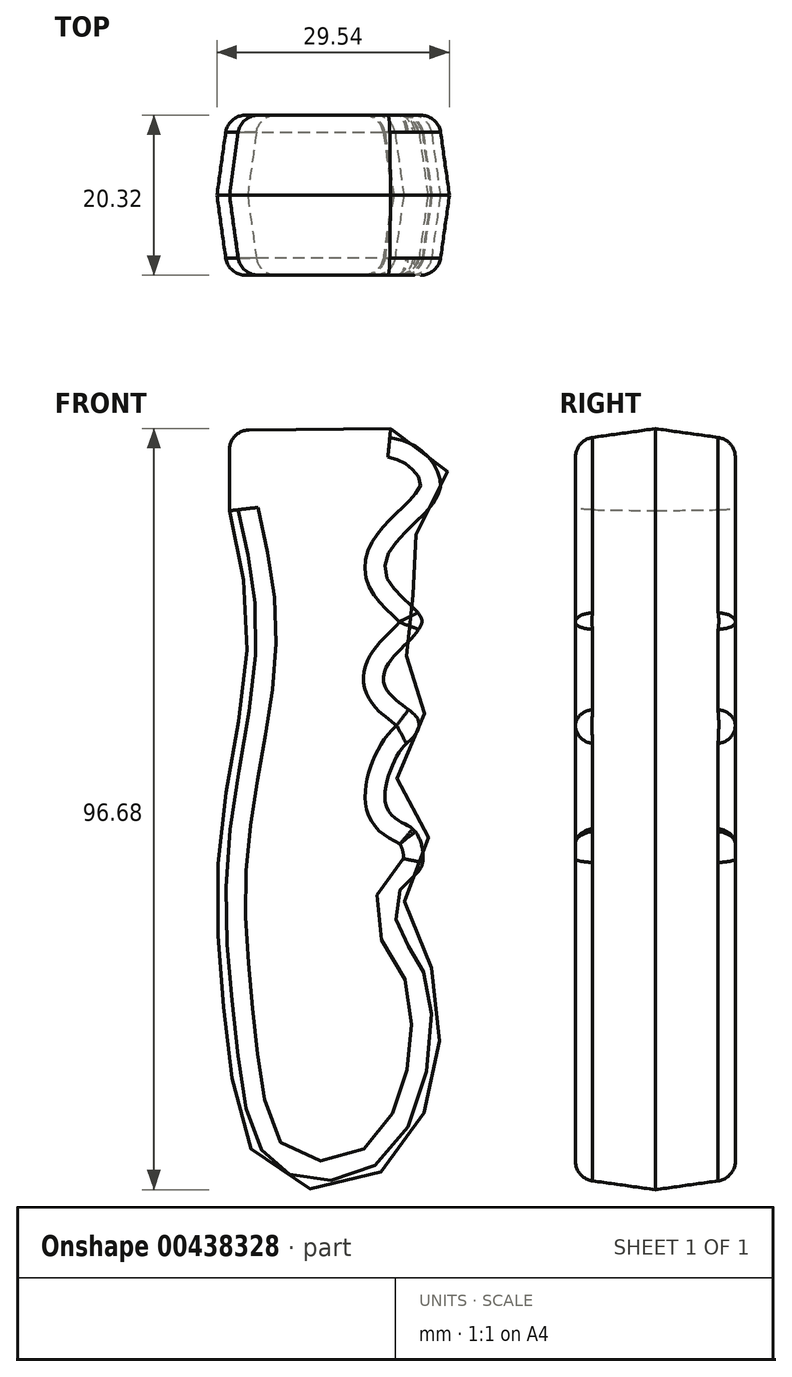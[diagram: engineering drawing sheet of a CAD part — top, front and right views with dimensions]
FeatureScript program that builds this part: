
annotation { "Feature Type Name" : "Feature", "Feature Type Description" : "" }
export const myFeature = defineFeature(function(context is Context, id is Id, definition is map)
    precondition{}
    {
        {
            var Q0;
            Q0=qCreatedBy(makeId("Front.planeOp"),FACE);
            var sketch = newSketch(context, id + "F0", { "sketchPlane" : qUnion([Q0])});
            skFitSpline(sketch, "E0", {"points": [v(-22.66, 35.36) * mm, v(-20.38, 18.1) * mm, v(-23.98, -7.68) * mm, v(-22.85, -32.52) * mm, v(-17.16, -49.01) * mm, v(-1.61, -47.11) * mm, v(3.5, -24.17) * mm, v(0, -17.73) * mm, v(0, -13.37) * mm, v(2.75, -10.33) * mm, v(1.61, -4.46) * mm, v(-1.61, -2) * mm, v(0, 4.27) * mm, v(1.8, 6.16) * mm, v(2.18, 9.57) * mm, v(-2, 14.12) * mm, v(2.94, 21.33) * mm, v(-1.8, 27.97) * mm, v(5.02, 37.26) * mm, v(2.18, 44.08) * mm, v(-2.18, 45.79) * mm], "startDerivative": vector(55.35, -239.01) * mm, "endDerivative": vector(-121.57, 24.5) * mm});
            skLineSegment(sketch, "E1", {"start": v(-22.66, 35.36) * mm, "end": v(-22.66, 45.6) * mm});
            skLineSegment(sketch, "E2", {"start": v(-22.66, 45.6) * mm, "end": v(-2.18, 45.79) * mm});
            skSolve(sketch);
        }
        {
            var Q0;
            Q0=makeQuery(id+"F0.imprint","IMPRINT",FACE,{"disambiguationData":[TD([[makeQuery(id+"F0.imprint","IMPRINT",EDGE,{"derivedFrom":sQuery(id+"F0.wireOp",EDGE,"E0")}),1.0]])]});
            extrude(context, id + "F1", {"entities" : qUnion([Q0]), "depth" : 10.16 * mm, "offsetDistance" : 25.4 * mm, "hasDraft" : true, "draftAngle" : 8 * degree, "draftPullDirection" : true, "hasSecondDirection" : true, "secondDirectionOppositeDirection" : true, "secondDirectionDepth" : 10.16 * mm, "hasSecondDirectionDraft" : true, "secondDirectionDraftAngle" : 8 * degree, "secondDirectionDraftPullDirection" : true});
        }
        {
            var Q0;
            Q0=makeQuery(id+"F1.opExtrude","CAP_EDGE",EDGE,{"disambiguationData":[OSD([sQuery(id+"F0.wireOp",EDGE,"E0")])],"isStart":true});
            var Q1;
            Q1=makeQuery(id+"F1.opExtrude","CAP_EDGE",EDGE,{"disambiguationData":[OSD([sQuery(id+"F0.wireOp",EDGE,"E2")])],"isStart":true});
            var Q2;
            Q2=makeQuery(id+"F1.opExtrude","CAP_EDGE",EDGE,{"disambiguationData":[OSD([sQuery(id+"F0.wireOp",EDGE,"E1")])],"isStart":true});
            var Q3;
            Q3=makeQuery(id+"F1.opExtrude","CAP_EDGE",EDGE,{"disambiguationData":[OSD([sQuery(id+"F0.wireOp",EDGE,"E0")])],"isStart":false});
            var Q4;
            Q4=makeQuery(id+"F1.opExtrude","CAP_EDGE",EDGE,{"disambiguationData":[OSD([sQuery(id+"F0.wireOp",EDGE,"E2")])],"isStart":false});
            var Q5;
            Q5=makeQuery(id+"F1.opExtrude","CAP_EDGE",EDGE,{"disambiguationData":[OSD([sQuery(id+"F0.wireOp",EDGE,"E1")])],"isStart":false});
            var Q6;
            Q6=makeQuery(id+"F1.*.split.splitOp","SPLIT",EDGE,{"derivedFrom":makeQuery(id+"F1.opExtrude","SWEPT_EDGE",EDGE,{"disambiguationData":[OSD([sQuery(id+"F0.wireOp",EDGE,"E1"),sQuery(id+"F0.wireOp",EDGE,"E2")])]}),"isFromBackBody":true});
            var Q7;
            Q7=makeQuery(id+"F1.*.split.splitOp","SPLIT",EDGE,{"derivedFrom":makeQuery(id+"F1.opExtrude","SWEPT_EDGE",EDGE,{"disambiguationData":[OSD([sQuery(id+"F0.wireOp",EDGE,"E1"),sQuery(id+"F0.wireOp",EDGE,"E2")])]})});
            fillet(context, id + "F2", {"entities" : qUnion([Q0, Q1, Q2, Q3, Q4, Q5, Q6, Q7]), "tangentPropagation" : true, "radius" : 2.54 * mm, "defaultsChanged" : false, "vertexSettings" : [], "allowEdgeOverflow" : false});
        }
    });
